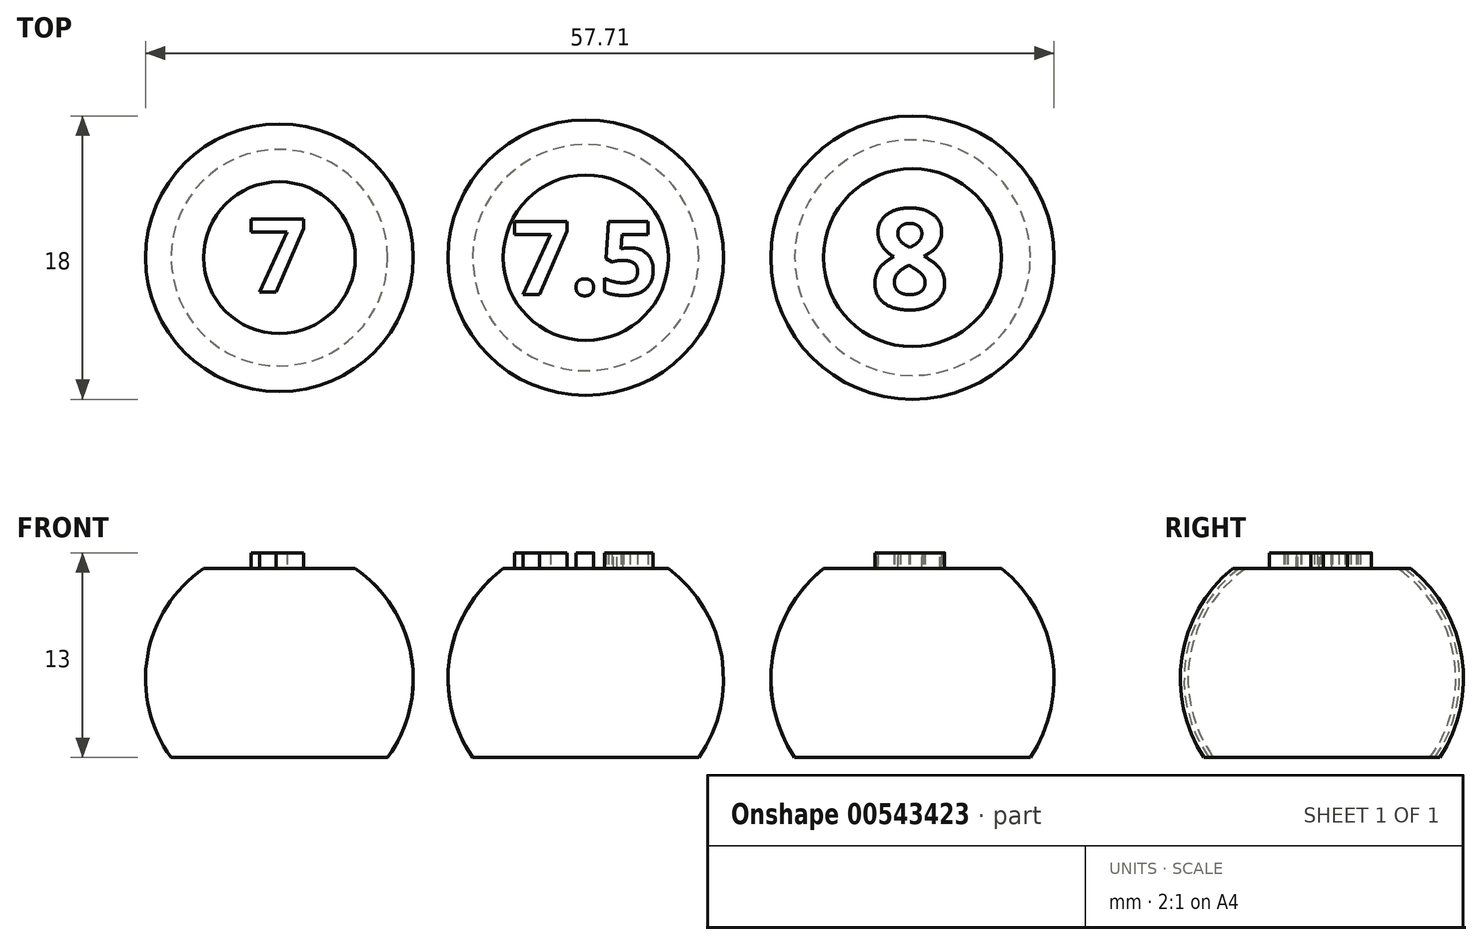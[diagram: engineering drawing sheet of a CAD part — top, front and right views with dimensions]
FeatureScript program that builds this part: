
annotation { "Feature Type Name" : "Feature", "Feature Type Description" : "" }
export const myFeature = defineFeature(function(context is Context, id is Id, definition is map)
    precondition{}
    {
        {
            var Q0;
            Q0=qCreatedBy(makeId("Front.planeOp"),FACE);
            var sketch = newSketch(context, id + "F0", { "sketchPlane" : qUnion([Q0])});
            skArc(sketch, "E0", {"start": v(-26, 12) * mm, "mid": v(-29.39, 6.4) * mm, "end": v(-27.93, 0) * mm});
            skArc(sketch, "E1", {"start": v(-5.66, 12) * mm, "mid": v(-8.9, 6.36) * mm, "end": v(-7.48, 0) * mm});
            skArc(sketch, "E2", {"start": v(-33.34, 0) * mm, "mid": v(-31.83, 6.43) * mm, "end": v(-35.4, 12) * mm});
            skLineSegment(sketch, "E3", {"start": v(7.48, 0) * mm, "end": v(-7.48, 0) * mm});
            skLineSegment(sketch, "E4", {"start": v(-45.03, 12) * mm, "end": v(-35.4, 12) * mm});
            skArc(sketch, "E5.trimOffspring", {"start": v(7.48, 0) * mm, "mid": v(8.9, 6.36) * mm, "end": v(5.66, 12) * mm});
            skLineSegment(sketch, "E6.trimOffspring", {"start": v(-5.66, 12) * mm, "end": v(5.66, 12) * mm});
            skLineSegment(sketch, "E7.trimOffspring", {"start": v(-13.57, 0) * mm, "end": v(-27.93, 0) * mm});
            skArc(sketch, "E8.trimOffspring", {"start": v(-13.57, 0) * mm, "mid": v(-12.11, 6.4) * mm, "end": v(-15.5, 12) * mm});
            skArc(sketch, "E9.trimOffspring", {"start": v(-45.03, 12) * mm, "mid": v(-48.6, 6.43) * mm, "end": v(-47.09, 0) * mm});
            skLineSegment(sketch, "E10.trimOffspring", {"start": v(-26, 12) * mm, "end": v(-15.5, 12) * mm});
            skLineSegment(sketch, "E11.trimOffspring", {"start": v(-33.34, 0) * mm, "end": v(-47.09, 0) * mm});
            skLineSegment(sketch, "E12", {"start": v(-40.21, 12) * mm, "end": v(-40.21, 0) * mm});
            skLineSegment(sketch, "E13", {"start": v(-20.75, 0) * mm, "end": v(-20.75, 12) * mm});
            skLineSegment(sketch, "E14", {"start": v(0, 0) * mm, "end": v(0, 12) * mm});
            skSolve(sketch);
        }
        {
            var Q0;
            {var subQ0=sQuery(id+"F0.wireOp",EDGE,"E2");Q0=makeQuery(id+"F0.imprint","IMPRINT",FACE,{"disambiguationData":[TD([[makeQuery(id+"F0.imprint","IMPRINT",EDGE,{"derivedFrom":subQ0}),1.0]])]});}
            var Q1;
            Q1=sQuery(id+"F0.wireOp",EDGE,"E12");
            revolve(context, id + "F1", {"entities" : qUnion([Q0]), "axis" : qUnion([Q1]), "revolveType" : RevolveType.FULL});
        }
        {
            var Q0;
            {var subQ0=sQuery(id+"F0.wireOp",EDGE,"E8.trimOffspring");Q0=makeQuery(id+"F0.imprint","IMPRINT",FACE,{"disambiguationData":[TD([[makeQuery(id+"F0.imprint","IMPRINT",EDGE,{"derivedFrom":subQ0}),1.0]])]});}
            var Q1;
            Q1=sQuery(id+"F0.wireOp",EDGE,"E13");
            revolve(context, id + "F2", {"entities" : qUnion([Q0]), "axis" : qUnion([Q1]), "revolveType" : RevolveType.FULL});
        }
        {
            var Q0;
            {var subQ0=sQuery(id+"F0.wireOp",EDGE,"E5.trimOffspring");Q0=makeQuery(id+"F0.imprint","IMPRINT",FACE,{"disambiguationData":[TD([[makeQuery(id+"F0.imprint","IMPRINT",EDGE,{"derivedFrom":subQ0}),1.0]])]});}
            var Q1;
            Q1=sQuery(id+"F0.wireOp",EDGE,"E14");
            revolve(context, id + "F3", {"entities" : qUnion([Q0]), "axis" : qUnion([Q1]), "revolveType" : RevolveType.FULL});
        }
        {
            var Q0;
            Q0=makeQuery(id+"F1.opRevolve","SWEPT_FACE",FACE,{"disambiguationData":[OSD([sQuery(id+"F0.wireOp",EDGE,"E4")])]});
            var sketch = newSketch(context, id + "F4", { "sketchPlane" : qUnion([Q0])});
            skText(sketch, "E15", { "text": "7", "fontName": "OpenSans-Bold.ttf"});
            const initialGuessF4  = {"E15": [-0.04218, -0.00219, 1, 0, 0.00469]};
            skSetInitialGuess(sketch, initialGuessF4);
            skSolve(sketch);
        }
        {
            var Q0;
            Q0=makeQuery(id+"F4.imprint","IMPRINT",FACE,{"disambiguationData":[TD([[makeQuery(id+"F4.imprint","IMPRINT",EDGE,{"derivedFrom":sQuery(id+"F4.wireOp",EDGE,"E15.sketch_text.stroke-0")}),-1.0]])]});
            extrude(context, id + "F5", {"entities" : qUnion([Q0]), "operationType" : NewBodyOperationType.ADD, "depth" : 1 * mm, "offsetDistance" : 25 * mm});
        }
        {
            var Q0;
            Q0=makeQuery(id+"F2.opRevolve","SWEPT_FACE",FACE,{"disambiguationData":[OSD([sQuery(id+"F0.wireOp",EDGE,"E10.trimOffspring")])]});
            var sketch = newSketch(context, id + "F6", { "sketchPlane" : qUnion([Q0])});
            skText(sketch, "E16", { "text": "7.5", "fontName": "OpenSans-Bold.ttf"});
            const initialGuessF6  = {"E16": [-0.02545, -0.00234, 1, 0, 0.00468]};
            skSetInitialGuess(sketch, initialGuessF6);
            skSolve(sketch);
        }
        {
            var Q0;
            Q0=makeQuery(id+"F6.imprint","IMPRINT",FACE,{"disambiguationData":[TD([[makeQuery(id+"F6.imprint","IMPRINT",EDGE,{"derivedFrom":sQuery(id+"F6.wireOp",EDGE,"E16.sketch_text.stroke-0")}),-1.0]])]});
            var Q1;
            Q1=makeQuery(id+"F6.imprint","IMPRINT",FACE,{"disambiguationData":[TD([[makeQuery(id+"F6.imprint","IMPRINT",EDGE,{"derivedFrom":sQuery(id+"F6.wireOp",EDGE,"E16.sketch_text.stroke-7")}),-1.0]])]});
            var Q2;
            Q2=makeQuery(id+"F6.imprint","IMPRINT",FACE,{"disambiguationData":[TD([[makeQuery(id+"F6.imprint","IMPRINT",EDGE,{"derivedFrom":sQuery(id+"F6.wireOp",EDGE,"E16.sketch_text.stroke-15")}),-1.0]])]});
            extrude(context, id + "F7", {"entities" : qUnion([Q0, Q1, Q2]), "operationType" : NewBodyOperationType.ADD, "depth" : 1 * mm, "offsetDistance" : 25 * mm});
        }
        {
            var Q0;
            Q0=makeQuery(id+"F3.opRevolve","SWEPT_FACE",FACE,{"disambiguationData":[OSD([sQuery(id+"F0.wireOp",EDGE,"E6.trimOffspring")])]});
            var sketch = newSketch(context, id + "F8", { "sketchPlane" : qUnion([Q0])});
            skText(sketch, "E17", { "text": "8", "fontName": "OpenSans-Bold.ttf"});
            const initialGuessF8  = {"E17": [-0.0027, -0.00324, 1, 0, 0.00637]};
            skSetInitialGuess(sketch, initialGuessF8);
            skSolve(sketch);
        }
        {
            var Q0;
            Q0=makeQuery(id+"F8.imprint","IMPRINT",FACE,{"disambiguationData":[TD([[makeQuery(id+"F8.imprint","IMPRINT",EDGE,{"derivedFrom":sQuery(id+"F8.wireOp",EDGE,"E17.sketch_text.stroke-0")}),-1.0]])]});
            extrude(context, id + "F9", {"entities" : qUnion([Q0]), "operationType" : NewBodyOperationType.ADD, "depth" : 1 * mm, "offsetDistance" : 25 * mm});
        }
    });
